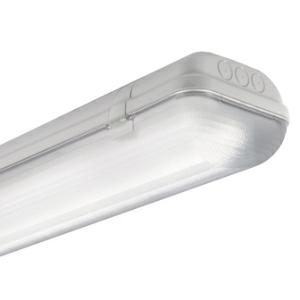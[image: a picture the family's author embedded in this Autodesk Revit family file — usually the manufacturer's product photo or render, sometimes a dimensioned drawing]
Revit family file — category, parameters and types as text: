
# Revit family: 3f_filippi_-_3f_linda_basic_3f_filippi_-_58763_-_3f_linda_led_basic_2x19w_l1270
name_source: partatom
category: Lighting Fixtures
units: mm (PartAtom-declared; Revit-internal decimal feet)

## family parameters
Cut with Voids When Loaded = No
Host = Face
Light Source = No
Part Type = Normal
Room Calculation Point = No
Round Connector Dimension = Use Diameter
Shared = No

## types (1)
- 3F Filippi - 3F Linda Basic (1 x LED, 5590 lm, 38 W, 4000 K)
    Apparent Load = 38 VA
    Approval mark = CE
    CIE Flux Codes = 46 76 93 97 100
    Color Rendering = 80
    Color Temperature = 4000 K
    Control Gear = Electronic ballast
    Default Elevation = 1800 mm
    Description = ILLUMINOTECHNICAL
Luminous efficiency 100% (DLOR 97%, ULOR 3%).
Initial luminous flux of the luminaire 5590 lm.
Controlled direct symmetric distribution.
Installation Interdistance Transv.D = 1.35 x hu - Long.D = 1.24 x hu.
Tabular UGR (CIE 117 - 4H-8H; S=0.25H; 70/50/20): RUG 23.2 - 22.3.
Beam angle: 94° - 78°.
Luminous efficacy 147 lm/W.
Lifetime (L92/B10): 30000 h. (tq+25°C)
Lifetime (L85/B10): 50000 h. (tq+25°C)
Lifetime (L75/B10): 80000 h. (tq+25°C)
Lifetime (L70/B10): 100000 h. (tq+25°C)
Lifetime (L75/B10): 50000 h. (tq+40°C)
Sudden decreased luminous flux after 50000 hours: 0% (C0).
Photobiological safety in compliance with IEC/TR 62778: RG0 risk exempt, (IEC 62471).
In compliance with IEC/EN 62722-2-1 - IEC/EN 62717 standards.

SOURCE
2 linear LED modules 19W/840.
Energy efficiency class (UE 2019/2020 - UE 2019/2015): D.
CIE 13.3 Colour rendering index: CRI >80 (R9 <50%).
IES TM-30 Fidelity Index: Rf = 84 Rg = 95.
CCT nominal colour temperature 4000 K.
Colour initial tolerance (MacAdam): SDCM 3.

MECHANICAL
Self-extinguishing V2 polycarbonate housing, injection moulded, RAL 7035 grey.
Ecologic anti-aging injected sealing gasket.
Diffuser in self-extinguishing V2 polycarbonate, photo-engraved interior, UV stabilised, injection moulded with smooth outer surface, tamper-proof opening.
Gear-holder reflector in hot-dip galvanised steel, painted with white polyester base.
Snug fit snap-lock clips for diffuser mounting, in polycarbonate.
Fixing brackets in stainless steel.
Possibility for technicians to access the interior of the luminaire.
Luminaire with limited surface temperature. - D - (EN 60598-2-24)
Dimensions: 1270x160 mm, height 100 mm. Weight 2.66 kg.
IP66 protection degree.
Mechanical strength to impacts IK10 (20 joule).
Glow-wire test resistance 850°C.

ELECTRICAL
Halogen Free electronic wiring 230V-50/60Hz, power factor 0.95, THD <25%, constant output current, SELV, class I, 1 driver.
Power of the luminaire 38 W.
ENEC - CE.
SAFE FLICKER: PstLM=<1 and SVM=<0.4 (IEC TR 61547-1 and IEC TR 63158), to ensure a more comfortable and safe light.
Luminaire compliant with EN 60598-2-22 for power supply from a centralised emergency system CPSS (Central Power Supply System), not incorporated in the luminaire - high risk areas excluded. The default power and flux are 100% in AC and 100% in DC.
Ambient temperature from -20°C to +40°C.
Temperature class T6 max 85°C.
Relative humidity UR: <85%.

INSTALLATION
Ceiling / Suspended / Wall.
All accessories dedicated to this product are available on the Catalog and on our website www.3F-Filippi.com.

APPLICATIONS
Suitable product for food production plants (HACCP), IFS (Food Version 6), BRC (GSFS Food Version 7).
Dry, dusty indoor environments, subject to occasional water splashes.
Virtually shatterproof polycarbonate compatibly with the fumes / atmospheres that compromise the elasticity of plastic materials.
Not suitable for installation on surfaces subject to important vibrations, exposed to weather conditions, on ropes or poles.
Suitable for illumination of public car parks and parking grounds referred to DIN 67528:2018-04.

WARNING
Fixture not suitable for cold stores with an ambient temperature <0°C and/or relative humidity >85%.
Luminaire designed for disposal/recycling at end-of-life.
Replaceable (LED only) light source by a professional. Replaceable control gear by a professional.
    Height = 100 mm  [stored 0.328084 ft]
    Lamp = 1 x LED
    Lamp Light Flux = 5590 lm
    Lamp Power = 38 W
    Lamp count = 1
    Length = 1270 mm
    Lifetime = 50000 h
    Luminous efficacy = 147 lm/W
    Manufacturer = 3F Filippi
    ModVariant = No
    Model = 3F Filippi - 58763 - 3F Linda LED Basic 2x19W L1270
    Mounting Place = Ceiling
    Mounting Type = Pendant
    Number of Poles = 1
    OnlyDefault = Yes
    Power Factor = 1
    Product Name = 3F Filippi - 3F Linda Basic
    Product group = pendant luminaire
    ProductGroupID = 9
    Protection Class = Protection class I
    Protection Degree = IP 66
    RLX_Detail_Level = 1
    RLX_Emergency_Light_Flux = 0 lm
    RLX_Emergency_Type = 0
    RLX_Emergency_Type_DB = No
    RlxData = <blob elided: 69985 chars, md5=b4d94369>
    Socket = socket
    Standby Power = 0 W
    System Light Flux = 5590 lm
    System Power = 38 W
    Type Comments = Product without accessories
    Type Image = 3ffilippi_3f_linda_led_basic_2x.jpg
    URL = http://relux.com
    VarID = ---
    Voltage = 0 V
    Weight = 0.00 kg
    Width = 160 mm

note: [stored X ft] marks values corroborated as IEEE doubles in the binary element streams (Revit-internal decimal feet)

## geometry (parser evidence)
native form markers: Blend x4, Sweep x8
no freeform markers — native parametric forms only
